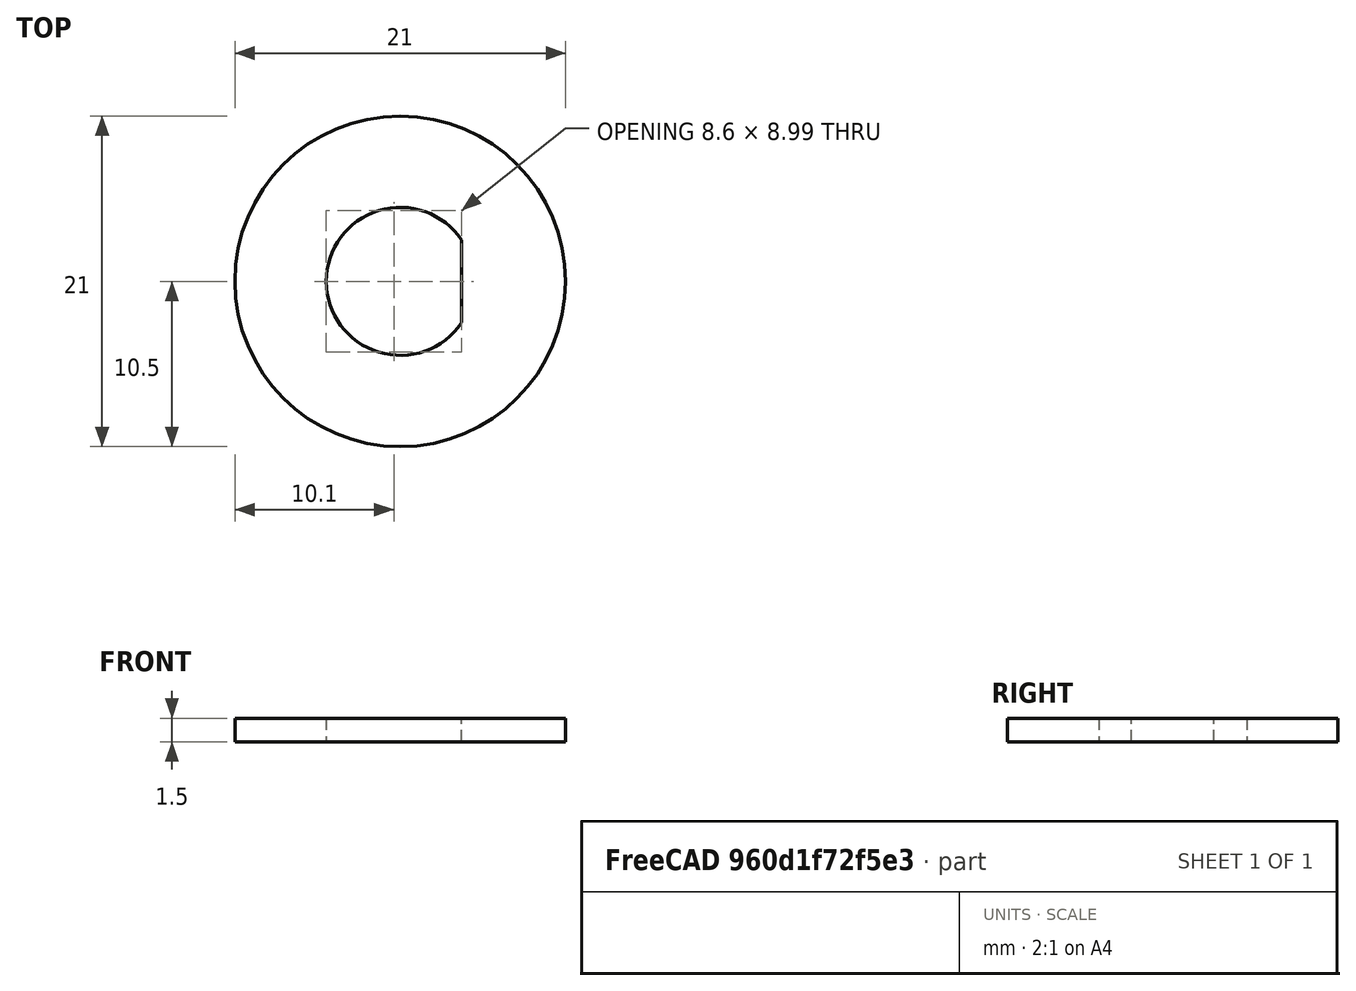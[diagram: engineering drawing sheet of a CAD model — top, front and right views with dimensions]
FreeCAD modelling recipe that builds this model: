
FCSTD DOCUMENT  (FreeCAD 0.19R24267 +99 (Git))
Label: BNC washer
License: All rights reserved
LicenseURL: http://en.wikipedia.org/wiki/All_rights_reserved
objects: Sketcher::SketchObject×1, PartDesign::Pad×1, PartDesign::Body×1
note: 4 computed .brp shape members not serialized (recipe doc carries the construction recipe); baked Part::Feature solids carry a one-line shape summary decoded from their .brp

FEATURE [Sketcher::SketchObject] Sketch
  FullyConstrained = true
  MapMode = 5
  Support = -> [XY_Plane]
  sketch-geometry (3):
    g0: Circle CenterX=0 CenterY=0 CenterZ=0 NormalX=0 NormalY=0 NormalZ=1 AngleXU=0 Radius=10.5
    g1: ArcOfCircle CenterX=0 CenterY=0 CenterZ=0 NormalX=0 NormalY=0 NormalZ=1 AngleXU=0 Radius=4.7 StartAngle=0.59207 EndAngle=5.69112
    g2: LineSegment StartX=3.9 StartY=2.62298 StartZ=0 EndX=3.9 EndY=-2.62298 EndZ=0
  constraints (8):
    c: Coincident(g0,g-1)
    c: Diameter(g0) = 21
    c: Coincident(g1,g0)
    c: Diameter(g1) = 9.4
    c: Vertical(g2)
    c: DistanceX(g0,g2) = 3.9
    c: Coincident(g1,g2)
    c: Coincident(g1,g2)
FEATURE [PartDesign::Pad] Pad
  Direction = (1,1,1)
  Length = 1.5
  Length2 = 100
  Profile = -> Sketch
  Type = 0
FEATURE [PartDesign::Body] Body
  Group = -> [Sketch,Pad]
  Origin = -> Origin
  Tip = -> Pad
